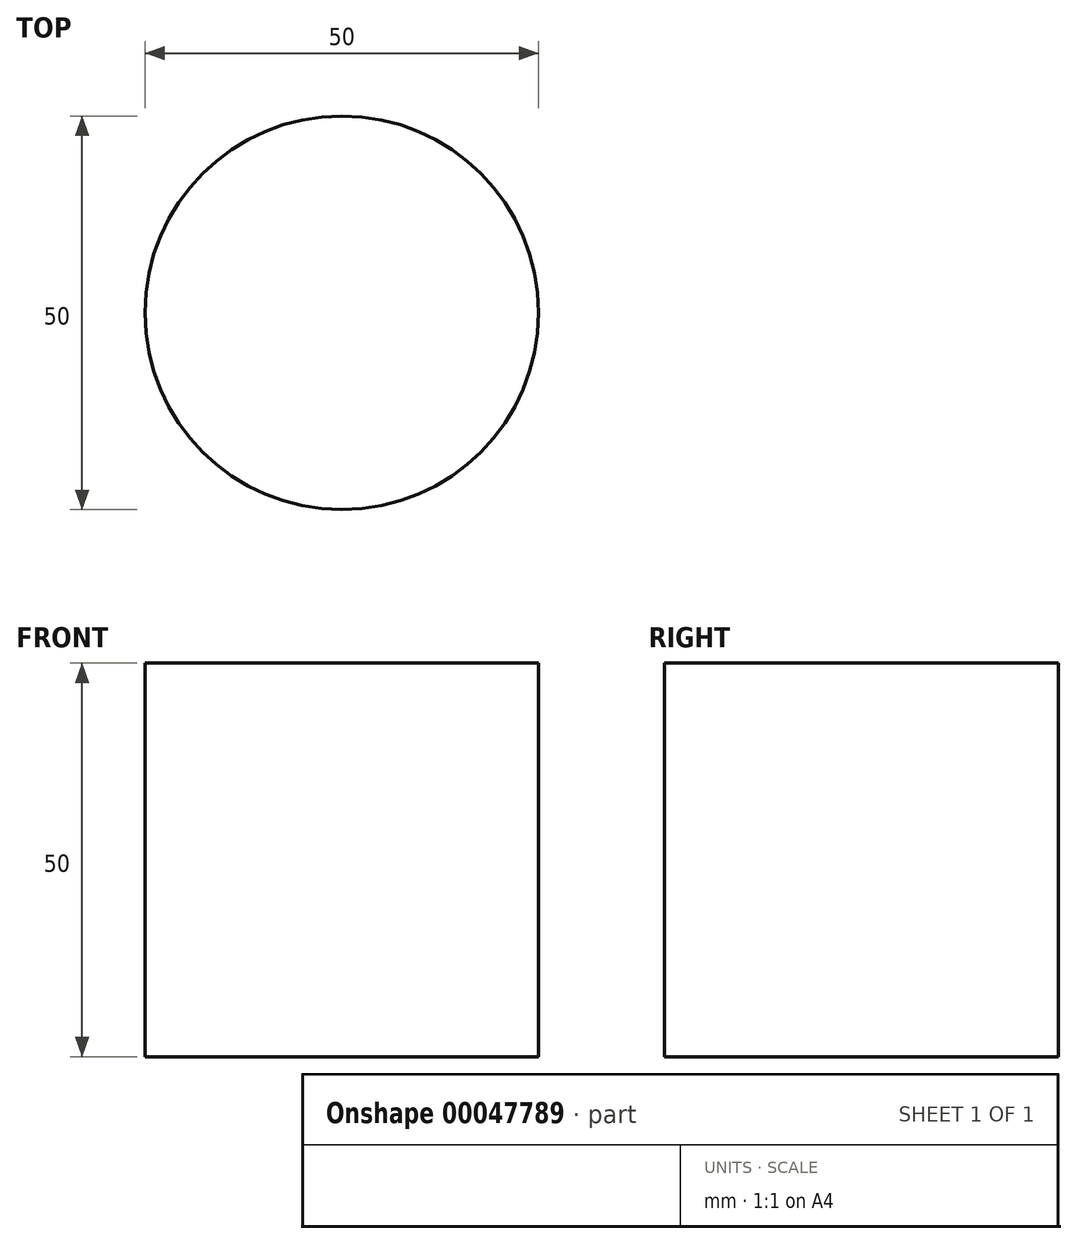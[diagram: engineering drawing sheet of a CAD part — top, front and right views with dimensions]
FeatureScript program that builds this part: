
annotation { "Feature Type Name" : "Feature", "Feature Type Description" : "" }
export const myFeature = defineFeature(function(context is Context, id is Id, definition is map)
    precondition{}
    {
        {
            var Q0;
            Q0=qCreatedBy(makeId("Top.planeOp"),FACE);
            var sketch = newSketch(context, id + "F0", { "sketchPlane" : qUnion([Q0])});
            skCircle(sketch, "E0", {"center": v(0, 0) * mm, "radius": 25 * mm});
            skSolve(sketch);
        }
        {
            var Q0;
            Q0=makeQuery(id+"F0.imprint","IMPRINT",FACE,{"disambiguationData":[TD([[makeQuery(id+"F0.imprint","IMPRINT",EDGE,{"derivedFrom":sQuery(id+"F0.wireOp",EDGE,"E0")}),1.0]])]});
            extrude(context, id + "F1", {"entities" : qUnion([Q0]), "depth" : 50 * mm});
        }
    });
